# Revit family: EL-AQ0622xxWSxxxMRM0700x
name_source: partatom
category: Oprawy oświetleniowe
units: mm (PartAtom-declared; Revit-internal decimal feet)

## family parameters
Numer OmniClass = 23.80.70.11
Obiekt nadrzędny = Powierzchnia
Punkt obliczania pomieszczeń = Nie
Tnij formami wycięć po wczytaniu = Nie
Typ części = Normalny
Tytuł OmniClass = Luminaries for Internal Lighting
Współdzielony = Nie
Wymiar okrągłego złącza = Użyj średnicy
Źródło światła = Tak

## types (4) — shared parameters
Emituj kształt widoczny w renderingu = Nie
Emituj z długości prostokąta = 408 mm
Emituj z szerokości prostokąta = 408 mm
Filtr koloru = 16777215
Kod zespołu = D5020200
Lampa = LED
Obciążenie pozorne = 58 VA
Odchylenie kierunku = 90.00°
Plik sieci fotometrycznej = EL-xxx_MRM.IES
Producent = RIDI Leuchten GmbH
URL = www.ridi.de
Zmiana temperatury barwowej przyciemniania lampy = <Brak>
brand = RIDI
conformity mark = CE
electrical safety class = 1
height = 60 mm  [stored 0.19685 ft]
ingress protection (IP) code = IP40
length = 630 mm  [stored 2.06693 ft]
nominal frequency = 50-60Hz
nominal voltage = 230
rated input power = 58
voltage type (AC, DC, UC) = AC
weight = 6,9 kg
width = 626 mm  [stored 2.05381 ft]
zero-valued in all types: Domyślna rzędna

## per-type parameters (varying)
| type | Model |
| EL-AQ0622NDWS830MRM0700-RF | 0627672 |
| EL-AQ0622DAWS830MRM0700 | 0637672 |
| EL-AQ0622NDWS840MRM0700-RF | 0627674 |
| EL-AQ0622DAWS840MRM0700 | 0637674 |

note: column(s) folded — value = type name in every type: product name

note: [stored X ft] marks values corroborated as IEEE doubles in the binary element streams (Revit-internal decimal feet)
